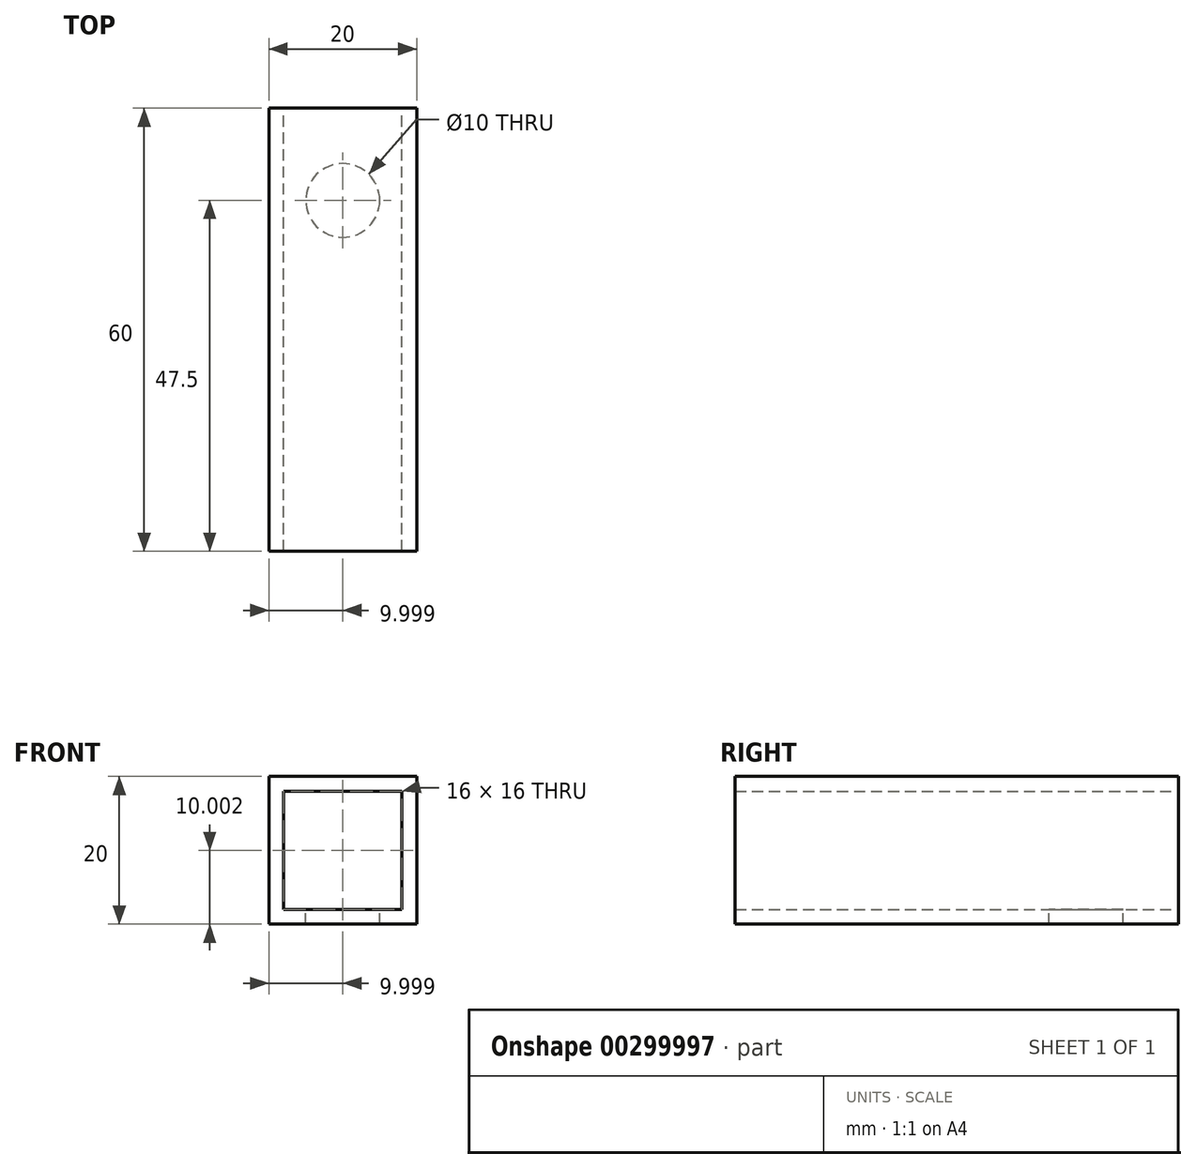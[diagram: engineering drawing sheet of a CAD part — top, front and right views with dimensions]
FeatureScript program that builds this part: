
annotation { "Feature Type Name" : "Feature", "Feature Type Description" : "" }
export const myFeature = defineFeature(function(context is Context, id is Id, definition is map)
    precondition{}
    {
        {
            var Q0;
            Q0=qCreatedBy(makeId("Front.planeOp"),FACE);
            var sketch = newSketch(context, id + "F0", { "sketchPlane" : qUnion([Q0])});
            skLineSegment(sketch, "E0.bottom", {"start": v(4.16, -4.1) * mm, "end": v(-15.84, -4.1) * mm});
            skLineSegment(sketch, "E0.top", {"start": v(4.16, 15.9) * mm, "end": v(-15.84, 15.9) * mm});
            skLineSegment(sketch, "E0.left", {"start": v(4.16, -4.1) * mm, "end": v(4.16, 15.9) * mm});
            skLineSegment(sketch, "E0.right", {"start": v(-15.84, -4.1) * mm, "end": v(-15.84, 15.9) * mm});
            skPoint(sketch, "E0.middle", {"position": v(-5.84, 5.9) * mm});
            skSolve(sketch);
        }
        {
            var Q0;
            Q0 = qSketchRegion(id + "F0", true);
            extrude(context, id + "F1", {"entities" : qUnion([Q0]), "depth" : 60 * mm});
        }
        {
            var Q0;
            Q0=makeQuery(id+"F1.opExtrude","CAP_FACE",FACE,{"disambiguationData":[OSD([sQuery(id+"F0.wireOp",EDGE,"E0.bottom"),sQuery(id+"F0.wireOp",EDGE,"E0.top"),sQuery(id+"F0.wireOp",EDGE,"E0.left"),sQuery(id+"F0.wireOp",EDGE,"E0.right")])],"isStart":true});
            var sketch = newSketch(context, id + "F2", { "sketchPlane" : qUnion([Q0])});
            skLineSegment(sketch, "E1.bottom", {"start": v(-2.16, -2.1) * mm, "end": v(13.84, -2.1) * mm});
            skLineSegment(sketch, "E1.top", {"start": v(-2.16, 13.9) * mm, "end": v(13.84, 13.9) * mm});
            skLineSegment(sketch, "E1.left", {"start": v(-2.16, -2.1) * mm, "end": v(-2.16, 13.9) * mm});
            skLineSegment(sketch, "E1.right", {"start": v(13.84, -2.1) * mm, "end": v(13.84, 13.9) * mm});
            skPoint(sketch, "E1.middle", {"position": v(5.84, 5.9) * mm});
            skPoint(sketch, "E1.middle.positionSnap0", {"position": v(5.84, 15.9) * mm});
            skPoint(sketch, "E1.middle.positionSnap1", {"position": v(15.84, 5.9) * mm});
            skPoint(sketch, "E1.centerSnap0", {"position": v(5.84, 15.9) * mm});
            skPoint(sketch, "E1.centerSnap1", {"position": v(15.84, 5.9) * mm});
            skSolve(sketch);
        }
        {
            var Q0;
            Q0 = qSketchRegion(id + "F2", true);
            extrude(context, id + "F3", {"entities" : qUnion([Q0]), "operationType" : NewBodyOperationType.REMOVE, "oppositeDirection" : true, "depth" : 25 * mm});
        }
        {
            var Q0;
            Q0=makeQuery(id+"F3.boolean.opBoolean","COPY",FACE,{"derivedFrom":makeQuery(id+"F3.opExtrude","SWEPT_FACE",FACE,{"disambiguationData":[OSD([sQuery(id+"F2.wireOp",EDGE,"E1.top")])]})});
            var sketch = newSketch(context, id + "F4", { "sketchPlane" : qUnion([Q0])});
            skCircle(sketch, "E2", {"center": v(-5.84, 12.5) * mm, "radius": 5 * mm});
            skPoint(sketch, "E2.centerSnap0", {"position": v(-13.84, 12.5) * mm});
            skPoint(sketch, "E2.centerSnap1", {"position": v(-5.84, 0) * mm});
            skSolve(sketch);
        }
        {
            var Q0;
            Q0 = qSketchRegion(id + "F4", true);
            extrude(context, id + "F5", {"entities" : qUnion([Q0]), "operationType" : NewBodyOperationType.REMOVE, "depth" : 25 * mm});
        }
        {
            var Q0;
            Q0=makeQuery(id+"F3.boolean.opBoolean","COPY",FACE,{"derivedFrom":makeQuery(id+"F3.opExtrude","CAP_FACE",FACE,{"disambiguationData":[OSD([sQuery(id+"F2.wireOp",EDGE,"E1.bottom"),sQuery(id+"F2.wireOp",EDGE,"E1.top"),sQuery(id+"F2.wireOp",EDGE,"E1.left"),sQuery(id+"F2.wireOp",EDGE,"E1.right")])],"isStart":false})});
            var sketch = newSketch(context, id + "F6", { "sketchPlane" : qUnion([Q0])});
            skLineSegment(sketch, "E3.bottom", {"start": v(13.84, -2.1) * mm, "end": v(-2.16, -2.1) * mm});
            skLineSegment(sketch, "E3.top", {"start": v(13.84, 13.9) * mm, "end": v(-2.16, 13.9) * mm});
            skLineSegment(sketch, "E3.left", {"start": v(13.84, -2.1) * mm, "end": v(13.84, 13.9) * mm});
            skLineSegment(sketch, "E3.right", {"start": v(-2.16, -2.1) * mm, "end": v(-2.16, 13.9) * mm});
            skPoint(sketch, "E3.middle", {"position": v(5.84, 5.9) * mm});
            skPoint(sketch, "E3.middle.positionSnap0", {"position": v(-2.16, 5.9) * mm});
            skPoint(sketch, "E3.middle.positionSnap1", {"position": v(5.84, 13.9) * mm});
            skPoint(sketch, "E3.centerSnap0", {"position": v(-2.16, 5.9) * mm});
            skPoint(sketch, "E3.centerSnap1", {"position": v(5.84, 13.9) * mm});
            skSolve(sketch);
        }
        {
            var Q0;
            Q0 = qSketchRegion(id + "F6", true);
            extrude(context, id + "F7", {"entities" : qUnion([Q0]), "operationType" : NewBodyOperationType.REMOVE, "endBound" : BoundingType.UP_TO_NEXT, "oppositeDirection" : true, "depth" : 25 * mm});
        }
    });
